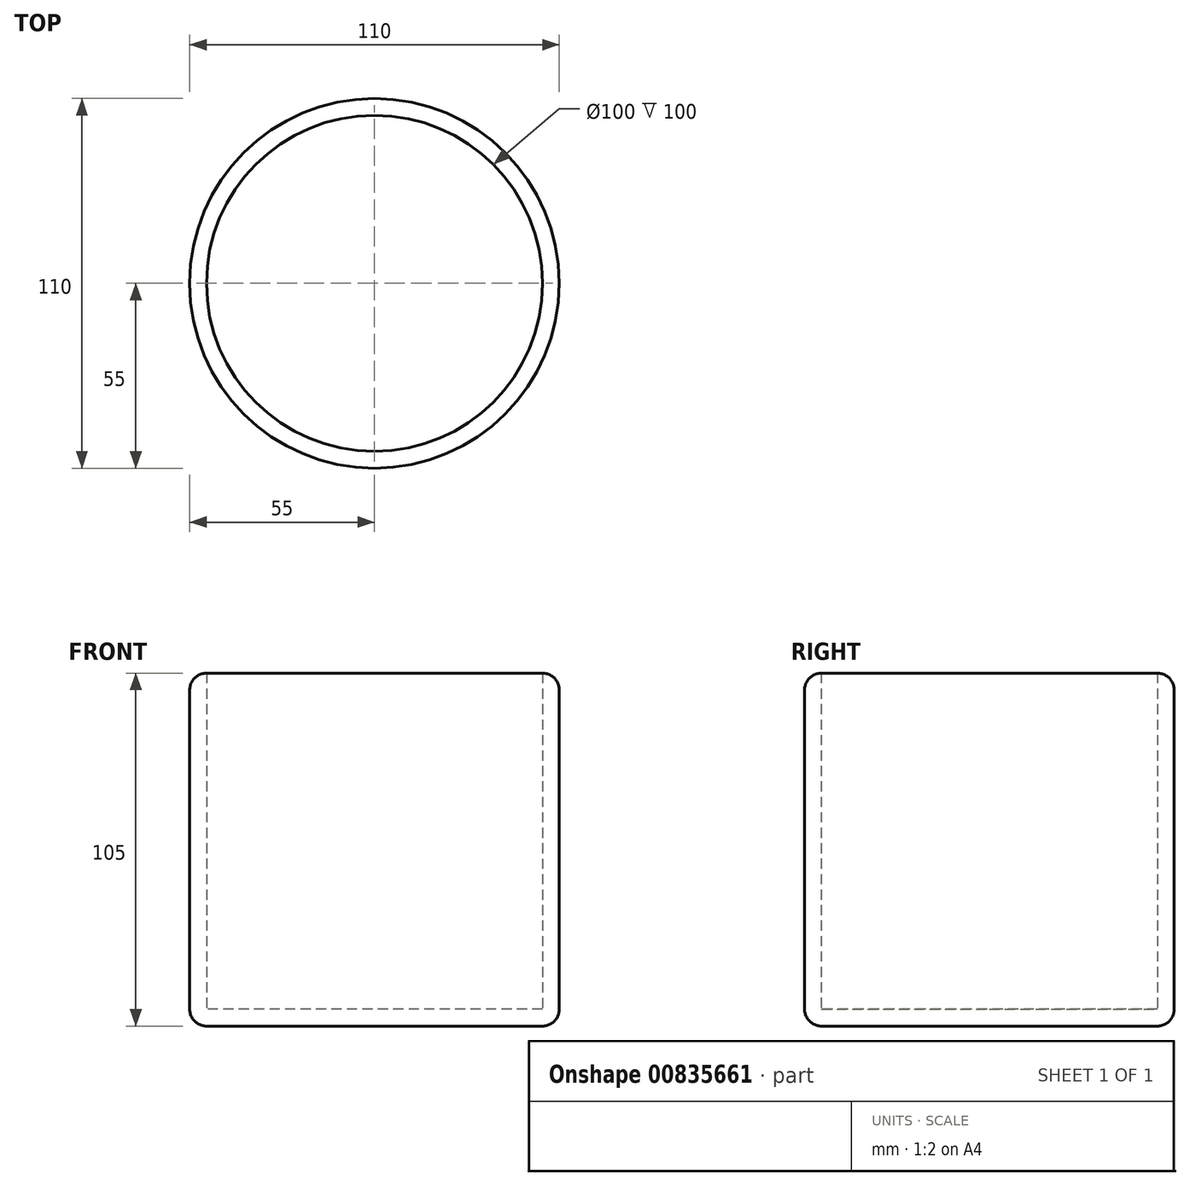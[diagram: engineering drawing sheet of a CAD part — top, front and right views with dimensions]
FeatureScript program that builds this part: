
annotation { "Feature Type Name" : "Feature", "Feature Type Description" : "" }
export const myFeature = defineFeature(function(context is Context, id is Id, definition is map)
    precondition{}
    {
        {
            var Q0;
            Q0=qCreatedBy(makeId("Top.planeOp"),FACE);
            var sketch = newSketch(context, id + "F0", { "sketchPlane" : qUnion([Q0])});
            skCircle(sketch, "E0", {"center": v(0, 0) * mm, "radius": 50 * mm});
            skSolve(sketch);
        }
        {
            var Q0;
            Q0=makeQuery(id+"F0.imprint","IMPRINT",FACE,{"disambiguationData":[TD([[makeQuery(id+"F0.imprint","IMPRINT",EDGE,{"derivedFrom":sQuery(id+"F0.wireOp",EDGE,"E0")}),1.0]])]});
            extrude(context, id + "F1", {"entities" : qUnion([Q0]), "depth" : 100 * mm, "offsetDistance" : 25 * mm});
        }
        {
            var Q0;
            Q0=makeQuery(id+"F1.opExtrude","CAP_FACE",FACE,{"disambiguationData":[OSD([sQuery(id+"F0.wireOp",EDGE,"E0")])],"isStart":false});
            shell(context, id + "F2", {"entities" : qUnion([Q0]), "thickness" : 5 * mm, "oppositeDirection" : true});
        }
        {
            var Q0;
            Q0=makeQuery(id+"F1.opExtrude","CAP_EDGE",EDGE,{"disambiguationData":[OSD([sQuery(id+"F0.wireOp",EDGE,"E0")])],"isStart":true});
            fillet(context, id + "F3", {"entities" : qUnion([Q0]), "radius" : 5 * mm, "tangentPropagation" : true, "allowEdgeOverflow" : false});
        }
        {
            var Q0;
            Q0=makeQuery(id+"F1.opExtrude","CAP_EDGE",EDGE,{"disambiguationData":[OSD([sQuery(id+"F0.wireOp",EDGE,"E0")])],"isStart":false});
            fillet(context, id + "F4", {"entities" : qUnion([Q0]), "radius" : 5 * mm, "tangentPropagation" : true, "allowEdgeOverflow" : false});
        }
    });
